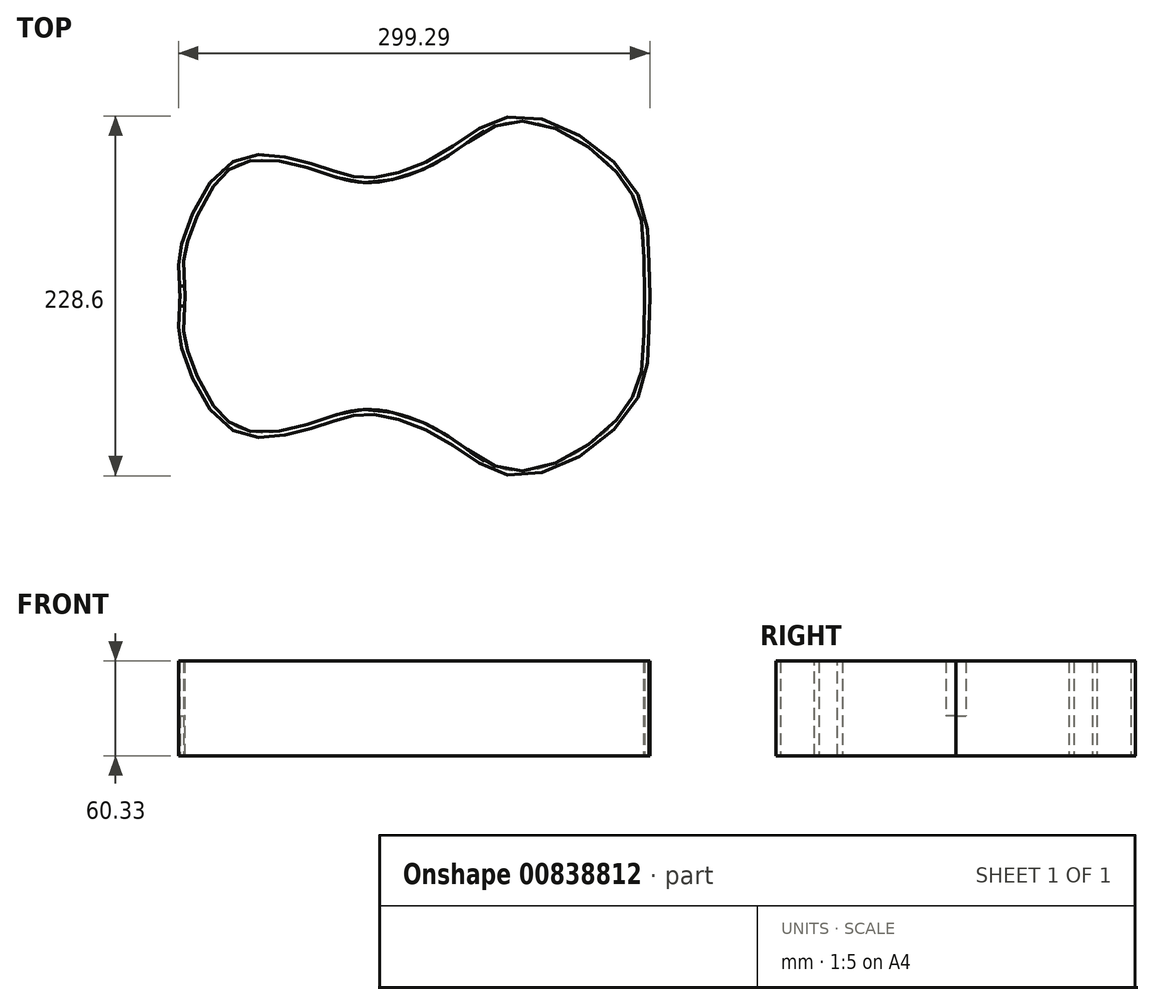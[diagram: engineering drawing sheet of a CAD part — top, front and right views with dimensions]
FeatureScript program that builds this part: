
annotation { "Feature Type Name" : "Feature", "Feature Type Description" : "" }
export const myFeature = defineFeature(function(context is Context, id is Id, definition is map)
    precondition{}
    {
        {
            var Q0;
            Q0=qCreatedBy(makeId("Top.planeOp"),FACE);
            var sketch = newSketch(context, id + "F0", { "sketchPlane" : qUnion([Q0])});
            skFitSpline(sketch, "E0", {"points": [v(-123.83, 0) * mm, v(-123.83, -28.13) * mm, v(-96, -81.4) * mm, v(-57.15, -88.27) * mm, v(-22.78, -78.36) * mm, v(0, -75.4) * mm, v(42.93, -90.56) * mm, v(92.08, -114.3) * mm, v(166.2, -65.98) * mm, v(174.63, 0) * mm], "startDerivative": vector(0, -540.72) * mm, "endDerivative": vector(49.2, 458.31) * mm});
            skFitSpline(sketch, "E1.MirrorCS", {"points": [v(-123.83, 0) * mm, v(-123.83, 28.13) * mm, v(-96, 81.4) * mm, v(-57.15, 88.27) * mm, v(-22.78, 78.36) * mm, v(0, 75.4) * mm, v(42.93, 90.56) * mm, v(92.08, 114.3) * mm, v(166.2, 65.98) * mm, v(174.63, 0) * mm], "startDerivative": vector(0, 540.72) * mm, "endDerivative": vector(49.2, -458.31) * mm});
            skFitSpline(sketch, "E2.0", {"points": [v(-120.65, 0) * mm, v(-120.65, 2.86) * mm, v(-120.78, 7.78) * mm, v(-121.14, 13.33) * mm, v(-121.46, 17.64) * mm, v(-121.52, 20.68) * mm, v(-121.36, 23.19) * mm, v(-121.13, 25.21) * mm, v(-120.73, 27.5) * mm, v(-120.15, 30.12) * mm, v(-119.4, 33.04) * mm, v(-118.46, 36.2) * mm, v(-117.36, 39.56) * mm, v(-115.68, 44.24) * mm, v(-113.2, 50.35) * mm, v(-109.68, 57.75) * mm, v(-105.67, 64.87) * mm, v(-102, 70.27) * mm, v(-98.9, 74.1) * mm, v(-96.5, 76.7) * mm, v(-94.47, 78.57) * mm, v(-92.83, 79.9) * mm, v(-91.16, 81.11) * mm, v(-89.05, 82.43) * mm, v(-85.6, 84.16) * mm, v(-81.13, 85.67) * mm, v(-75.54, 86.57) * mm, v(-69.76, 86.7) * mm, v(-63.85, 86.21) * mm, v(-58.88, 85.4) * mm, v(-54.92, 84.57) * mm, v(-51, 83.66) * mm, v(-44.2, 81.86) * mm, v(-36.73, 79.5) * mm, v(-29.7, 77.2) * mm, v(-24.7, 75.6) * mm, v(-19.97, 74.2) * mm, v(-15.38, 73.09) * mm, v(-10.74, 72.3) * mm, v(-5.92, 71.95) * mm, v(-0.77, 72.07) * mm, v(4.85, 72.72) * mm, v(10.87, 73.9) * mm, v(17.2, 75.57) * mm, v(23.74, 77.73) * mm, v(30.39, 80.39) * mm, v(35.92, 83) * mm, v(40.3, 85.33) * mm, v(43.54, 87.2) * mm, v(46.72, 89.17) * mm, v(49.83, 91.23) * mm, v(52.87, 93.34) * mm, v(56.87, 96.16) * mm, v(61.79, 99.64) * mm, v(67.68, 103.5) * mm, v(73.66, 106.8) * mm, v(79.84, 109.33) * mm, v(85.24, 110.64) * mm, v(89.81, 111.12) * mm, v(94.57, 111.17) * mm, v(101, 110.4) * mm, v(109.24, 108.22) * mm, v(117.73, 104.9) * mm, v(126.24, 100.58) * mm, v(134.55, 95.38) * mm, v(142.43, 89.43) * mm, v(149.65, 82.9) * mm, v(154.94, 77.07) * mm, v(158.62, 72.27) * mm, v(161.1, 68.6) * mm, v(163.24, 64.92) * mm, v(165.04, 61.22) * mm, v(166.54, 57.47) * mm, v(168.16, 52.43) * mm, v(169.57, 46.04) * mm, v(170.5, 38.28) * mm, v(170.98, 27.85) * mm, v(170.75, 14.8) * mm, v(170.94, 4.63) * mm, v(171.47, -0.34) * mm]});
            skFitSpline(sketch, "E3.0", {"points": [v(-120.65, 0) * mm, v(-120.65, -2.86) * mm, v(-120.78, -7.78) * mm, v(-121.14, -13.33) * mm, v(-121.46, -17.64) * mm, v(-121.52, -20.68) * mm, v(-121.36, -23.19) * mm, v(-121.13, -25.21) * mm, v(-120.73, -27.5) * mm, v(-120.15, -30.12) * mm, v(-119.4, -33.04) * mm, v(-118.46, -36.2) * mm, v(-117.36, -39.56) * mm, v(-115.68, -44.24) * mm, v(-113.2, -50.35) * mm, v(-109.68, -57.75) * mm, v(-105.67, -64.87) * mm, v(-102, -70.27) * mm, v(-98.9, -74.1) * mm, v(-96.5, -76.7) * mm, v(-94.47, -78.57) * mm, v(-92.83, -79.9) * mm, v(-91.16, -81.11) * mm, v(-89.05, -82.43) * mm, v(-85.6, -84.16) * mm, v(-81.13, -85.67) * mm, v(-75.54, -86.57) * mm, v(-69.76, -86.7) * mm, v(-63.85, -86.21) * mm, v(-58.88, -85.4) * mm, v(-54.92, -84.57) * mm, v(-51, -83.66) * mm, v(-44.2, -81.86) * mm, v(-36.73, -79.5) * mm, v(-29.7, -77.2) * mm, v(-24.7, -75.6) * mm, v(-19.97, -74.2) * mm, v(-15.38, -73.09) * mm, v(-10.74, -72.3) * mm, v(-5.92, -71.95) * mm, v(-0.77, -72.07) * mm, v(4.85, -72.72) * mm, v(10.87, -73.9) * mm, v(17.2, -75.57) * mm, v(23.74, -77.73) * mm, v(30.39, -80.39) * mm, v(35.92, -83) * mm, v(40.3, -85.33) * mm, v(43.54, -87.2) * mm, v(46.72, -89.17) * mm, v(49.83, -91.23) * mm, v(52.87, -93.34) * mm, v(56.87, -96.16) * mm, v(61.79, -99.64) * mm, v(67.68, -103.5) * mm, v(73.66, -106.8) * mm, v(79.84, -109.33) * mm, v(85.24, -110.64) * mm, v(89.81, -111.12) * mm, v(94.57, -111.17) * mm, v(101, -110.4) * mm, v(109.24, -108.22) * mm, v(117.73, -104.9) * mm, v(126.24, -100.58) * mm, v(134.55, -95.38) * mm, v(142.43, -89.43) * mm, v(149.65, -82.9) * mm, v(154.94, -77.07) * mm, v(158.62, -72.27) * mm, v(161.1, -68.6) * mm, v(163.24, -64.92) * mm, v(165.04, -61.22) * mm, v(166.54, -57.47) * mm, v(168.16, -52.43) * mm, v(169.57, -46.04) * mm, v(170.5, -38.28) * mm, v(170.98, -27.85) * mm, v(170.75, -14.8) * mm, v(170.94, -4.63) * mm, v(171.47, 0.34) * mm]});
            skSolve(sketch);
        }
        {
            var Q0;
            Q0 = qSketchRegion(id + "F0", true);
            extrude(context, id + "F1", {"entities" : qUnion([Q0]), "depth" : 60.32 * mm, "offsetDistance" : 25.4 * mm});
        }
        {
            var Q0;
            Q0=qCreatedBy(makeId("Right.planeOp"),FACE);
            var sketch = newSketch(context, id + "F2", { "sketchPlane" : qUnion([Q0])});
            skLineSegment(sketch, "E4.bottom", {"start": v(6.35, 60.33) * mm, "end": v(-6.35, 60.33) * mm});
            skLineSegment(sketch, "E4.top", {"start": v(6.35, 25.4) * mm, "end": v(-6.35, 25.4) * mm});
            skLineSegment(sketch, "E4.left", {"start": v(6.35, 60.33) * mm, "end": v(6.35, 25.4) * mm});
            skLineSegment(sketch, "E4.right", {"start": v(-6.35, 60.33) * mm, "end": v(-6.35, 25.4) * mm});
            skSolve(sketch);
        }
        {
            var Q0;
            Q0 = qSketchRegion(id + "F2", true);
            extrude(context, id + "F3", {"entities" : qUnion([Q0]), "operationType" : NewBodyOperationType.REMOVE, "oppositeDirection" : true, "depth" : 174 * mm, "offsetDistance" : 25.4 * mm});
        }
    });
